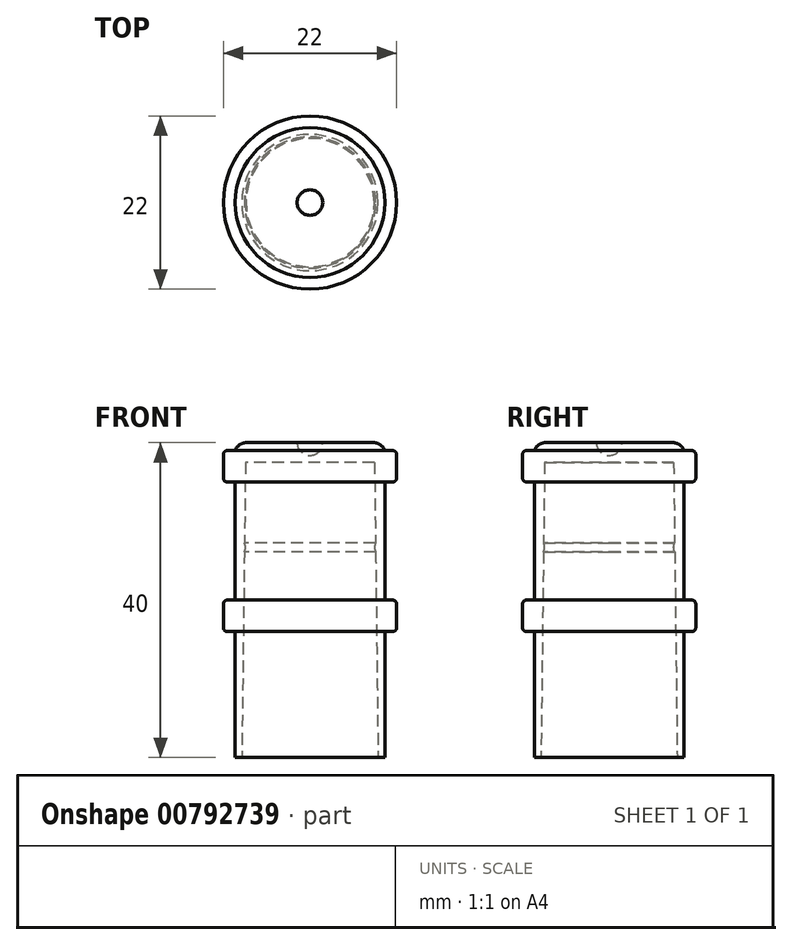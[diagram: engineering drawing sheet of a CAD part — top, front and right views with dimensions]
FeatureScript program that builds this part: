
annotation { "Feature Type Name" : "Feature", "Feature Type Description" : "" }
export const myFeature = defineFeature(function(context is Context, id is Id, definition is map)
    precondition{}
    {
        {
            var Q0;
            Q0=qCreatedBy(makeId("Front.planeOp"),FACE);
            var sketch = newSketch(context, id + "F0", { "sketchPlane" : qUnion([Q0])});
            skLineSegment(sketch, "E0", {"start": v(0, 20) * mm, "end": v(0, -20) * mm, "construction": true});
            skLineSegment(sketch, "E1", {"start": v(0, 20) * mm, "end": v(9.5, 20) * mm});
            skLineSegment(sketch, "E2", {"start": v(9.5, 20) * mm, "end": v(9.5, 19) * mm});
            skLineSegment(sketch, "E3", {"start": v(9.5, 19) * mm, "end": v(10.5, 19) * mm});
            skLineSegment(sketch, "E4", {"start": v(11, 18.5) * mm, "end": v(11, 15.5) * mm});
            skLineSegment(sketch, "E5", {"start": v(10.5, 15) * mm, "end": v(9.5, 15) * mm});
            skLineSegment(sketch, "E6", {"start": v(9.5, 15) * mm, "end": v(9.5, 0) * mm});
            skLineSegment(sketch, "E7", {"start": v(9.5, 0) * mm, "end": v(10.5, 0) * mm});
            skLineSegment(sketch, "E8", {"start": v(11, -0.5) * mm, "end": v(11, -3.5) * mm});
            skLineSegment(sketch, "E9", {"start": v(10.5, -4) * mm, "end": v(9.5, -4) * mm});
            skLineSegment(sketch, "E10", {"start": v(9.5, -4) * mm, "end": v(9.5, -20) * mm});
            skLineSegment(sketch, "E11", {"start": v(9.5, -20) * mm, "end": v(0, -20) * mm});
            skPoint(sketch, "E12.visualSharp", {"position": v(11, 0) * mm});
            skArc(sketch, "E12.filletArc", {"start": v(11, -0.5) * mm, "mid": v(10.85, -0.15) * mm, "end": v(10.5, 0) * mm});
            skPoint(sketch, "E13.visualSharp", {"position": v(11, -4) * mm});
            skArc(sketch, "E13.filletArc", {"start": v(10.5, -4) * mm, "mid": v(10.85, -3.85) * mm, "end": v(11, -3.5) * mm});
            skPoint(sketch, "E14.visualSharp", {"position": v(11, 19) * mm});
            skArc(sketch, "E14.filletArc", {"start": v(11, 18.5) * mm, "mid": v(10.85, 18.85) * mm, "end": v(10.5, 19) * mm});
            skPoint(sketch, "E15.visualSharp", {"position": v(11, 15) * mm});
            skArc(sketch, "E15.filletArc", {"start": v(10.5, 15) * mm, "mid": v(10.85, 15.15) * mm, "end": v(11, 15.5) * mm});
            skLineSegment(sketch, "E16", {"start": v(0, 17.5) * mm, "end": v(8.2, 17.5) * mm});
            skLineSegment(sketch, "E17", {"start": v(0, -20) * mm, "end": v(8.65, -20) * mm});
            skLineSegment(sketch, "E18", {"start": v(8.2, 17.5) * mm, "end": v(8.32, 7.25) * mm});
            skArc(sketch, "E19", {"start": v(0, 18.38) * mm, "mid": v(1.15, 18.85) * mm, "end": v(1.62, 20) * mm});
            skPoint(sketch, "E20", {"position": v(0, 0) * mm});
            skLineSegment(sketch, "E21", {"start": v(0, 18.38) * mm, "end": v(0, -20) * mm});
            skLineSegment(sketch, "E22", {"start": v(0, 6.7) * mm, "end": v(8.33, 6.7) * mm, "construction": true});
            skArc(sketch, "E23", {"start": v(8.32, 7.25) * mm, "mid": v(8.2, 6.68) * mm, "end": v(8.34, 6.12) * mm});
            skLineSegment(sketch, "E24.trimOffspring", {"start": v(8.34, 6.12) * mm, "end": v(8.65, -20) * mm});
            skSolve(sketch);
        }
        {
            var Q0;
            {var subQ0=sQuery(id+"F0.wireOp",EDGE,"E2");Q0=makeQuery(id+"F0.imprint","IMPRINT",FACE,{"disambiguationData":[TD([[makeQuery(id+"F0.imprint","IMPRINT",EDGE,{"derivedFrom":subQ0}),-1.0]])]});}
            var Q1;
            Q1=sQuery(id+"F0.wireOp",EDGE,"E0");
            revolve(context, id + "F1", {"surfaceOperationType" : NewSurfaceOperationType.NEW, "entities" : qUnion([Q0]), "axis" : qUnion([Q1]), "revolveType" : RevolveType.FULL});
        }
        {
            var Q0;
            Q0=makeQuery(id+"F1.opRevolve","SWEPT_EDGE",EDGE,{"disambiguationData":[OSD([sQuery(id+"F0.wireOp",EDGE,"E1"),sQuery(id+"F0.wireOp",EDGE,"E2")])]});
            fillet(context, id + "F2", {"entities" : qUnion([Q0]), "radius" : 1.5 * mm, "tangentPropagation" : true, "allowEdgeOverflow" : false});
        }
    });
